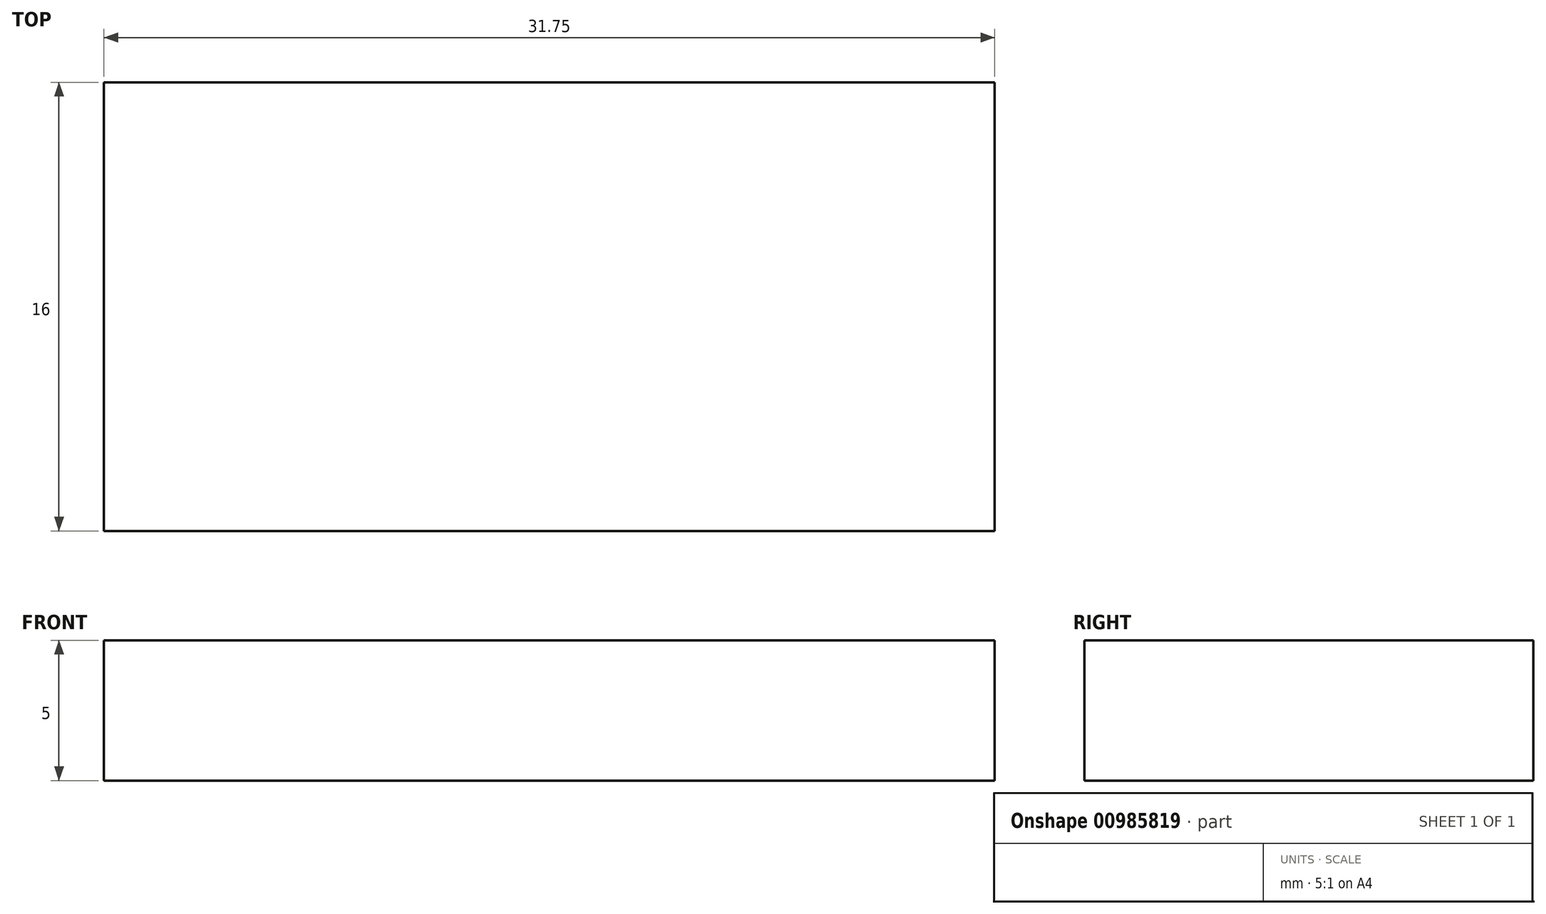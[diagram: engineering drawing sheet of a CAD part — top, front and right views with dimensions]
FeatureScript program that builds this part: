
annotation { "Feature Type Name" : "Feature", "Feature Type Description" : "" }
export const myFeature = defineFeature(function(context is Context, id is Id, definition is map)
    precondition{}
    {
        {
            var Q0;
            Q0=qCreatedBy(makeId("Top.planeOp"),FACE);
            var sketch = newSketch(context, id + "F0", { "sketchPlane" : qUnion([Q0])});
            skLineSegment(sketch, "E0.bottom", {"start": v(0, 0) * mm, "end": v(0, 0) * mm});
            skLineSegment(sketch, "E0.top", {"start": v(0, 0) * mm, "end": v(0, 0) * mm});
            skLineSegment(sketch, "E0.left", {"start": v(0, 0) * mm, "end": v(0, 0) * mm});
            skLineSegment(sketch, "E0.right", {"start": v(0, 0) * mm, "end": v(0, 0) * mm});
            skLineSegment(sketch, "E1.bottom", {"start": v(31.75, 16) * mm, "end": v(0, 16) * mm});
            skLineSegment(sketch, "E1.top", {"start": v(31.75, 0) * mm, "end": v(0, 0) * mm});
            skLineSegment(sketch, "E1.left", {"start": v(31.75, 16) * mm, "end": v(31.75, 0) * mm});
            skLineSegment(sketch, "E1.right", {"start": v(0, 16) * mm, "end": v(0, 0) * mm});
            skSolve(sketch);
        }
        {
            var Q0;
            Q0=makeQuery(id+"F0.imprint","IMPRINT",FACE,{"disambiguationData":[TD([[makeQuery(id+"F0.imprint","IMPRINT",EDGE,{"derivedFrom":sQuery(id+"F0.wireOp",EDGE,"E1.bottom")}),1.0]])]});
            extrude(context, id + "F1", {"entities" : qUnion([Q0]), "depth" : 5 * mm, "offsetDistance" : 25.4 * mm});
        }
    });
